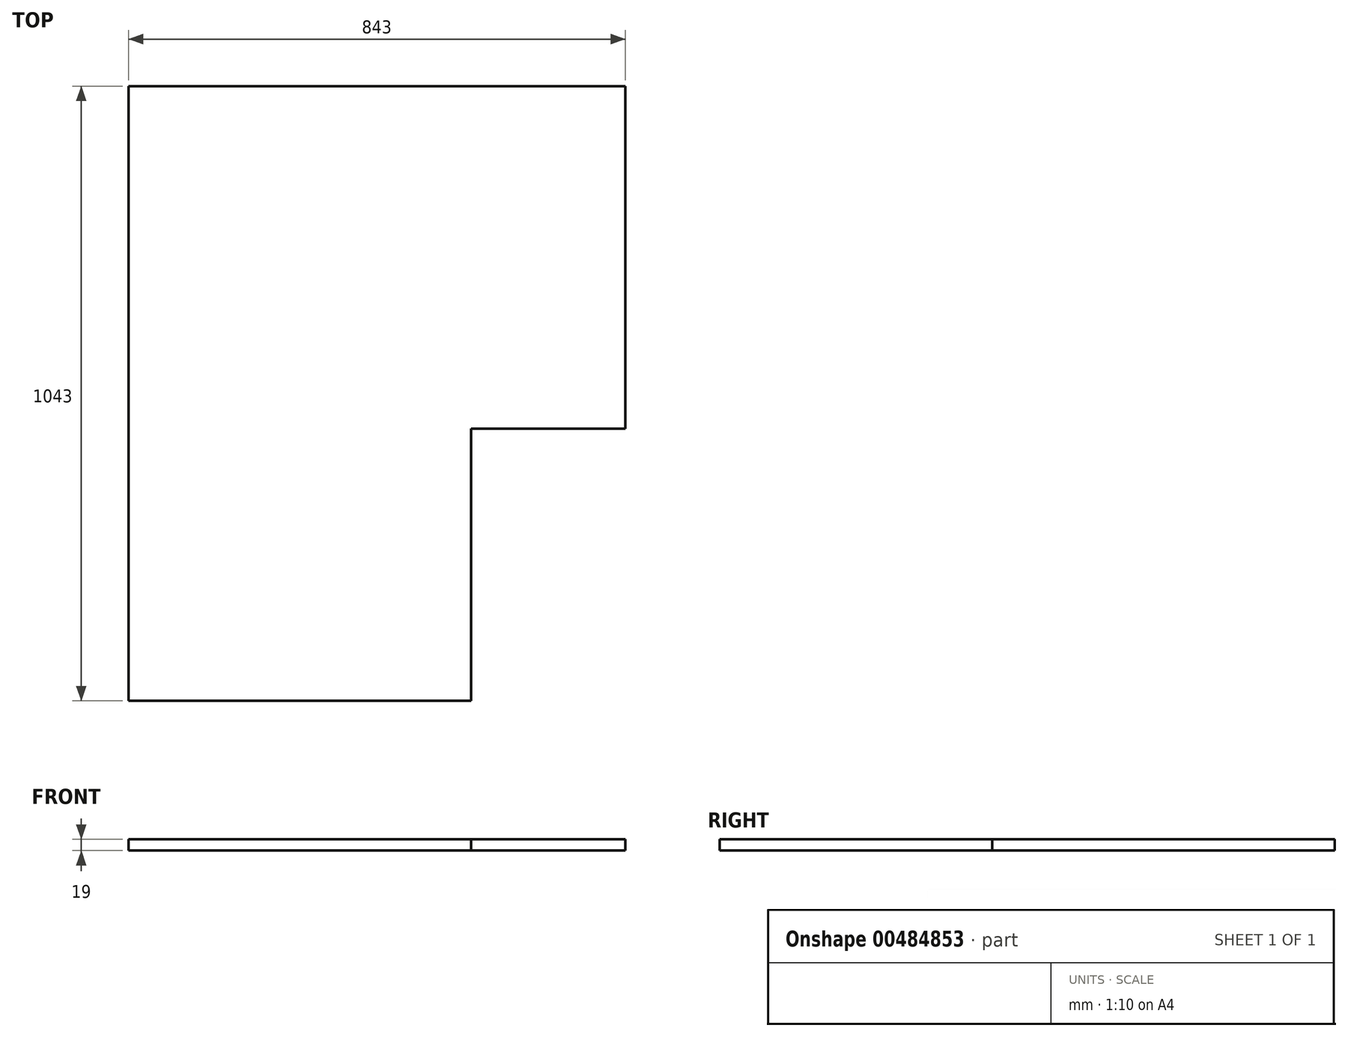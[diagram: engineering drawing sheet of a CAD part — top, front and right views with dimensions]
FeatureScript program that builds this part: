
annotation { "Feature Type Name" : "Feature", "Feature Type Description" : "" }
export const myFeature = defineFeature(function(context is Context, id is Id, definition is map)
    precondition{}
    {
        {
            var Q0;
            Q0=qCreatedBy(makeId("Top.planeOp"),FACE);
            var sketch = newSketch(context, id + "F0", { "sketchPlane" : qUnion([Q0])});
            skLineSegment(sketch, "E0", {"start": v(-459.8, 432.1) * mm, "end": v(-459.8, -610.9) * mm});
            skLineSegment(sketch, "E1", {"start": v(-459.8, 432.1) * mm, "end": v(383.2, 432.1) * mm});
            skLineSegment(sketch, "E2", {"start": v(383.2, 432.1) * mm, "end": v(383.2, -148.9) * mm});
            skLineSegment(sketch, "E3", {"start": v(383.2, -148.9) * mm, "end": v(121.2, -148.9) * mm});
            skLineSegment(sketch, "E4", {"start": v(121.2, -148.9) * mm, "end": v(121.2, -610.9) * mm});
            skLineSegment(sketch, "E5", {"start": v(-459.8, -610.9) * mm, "end": v(121.2, -610.9) * mm});
            skSolve(sketch);
        }
        {
            var Q0;
            Q0 = qSketchRegion(id + "F0", true);
            extrude(context, id + "F1", {"entities" : qUnion([Q0]), "depth" : 19 * mm});
        }
    });
